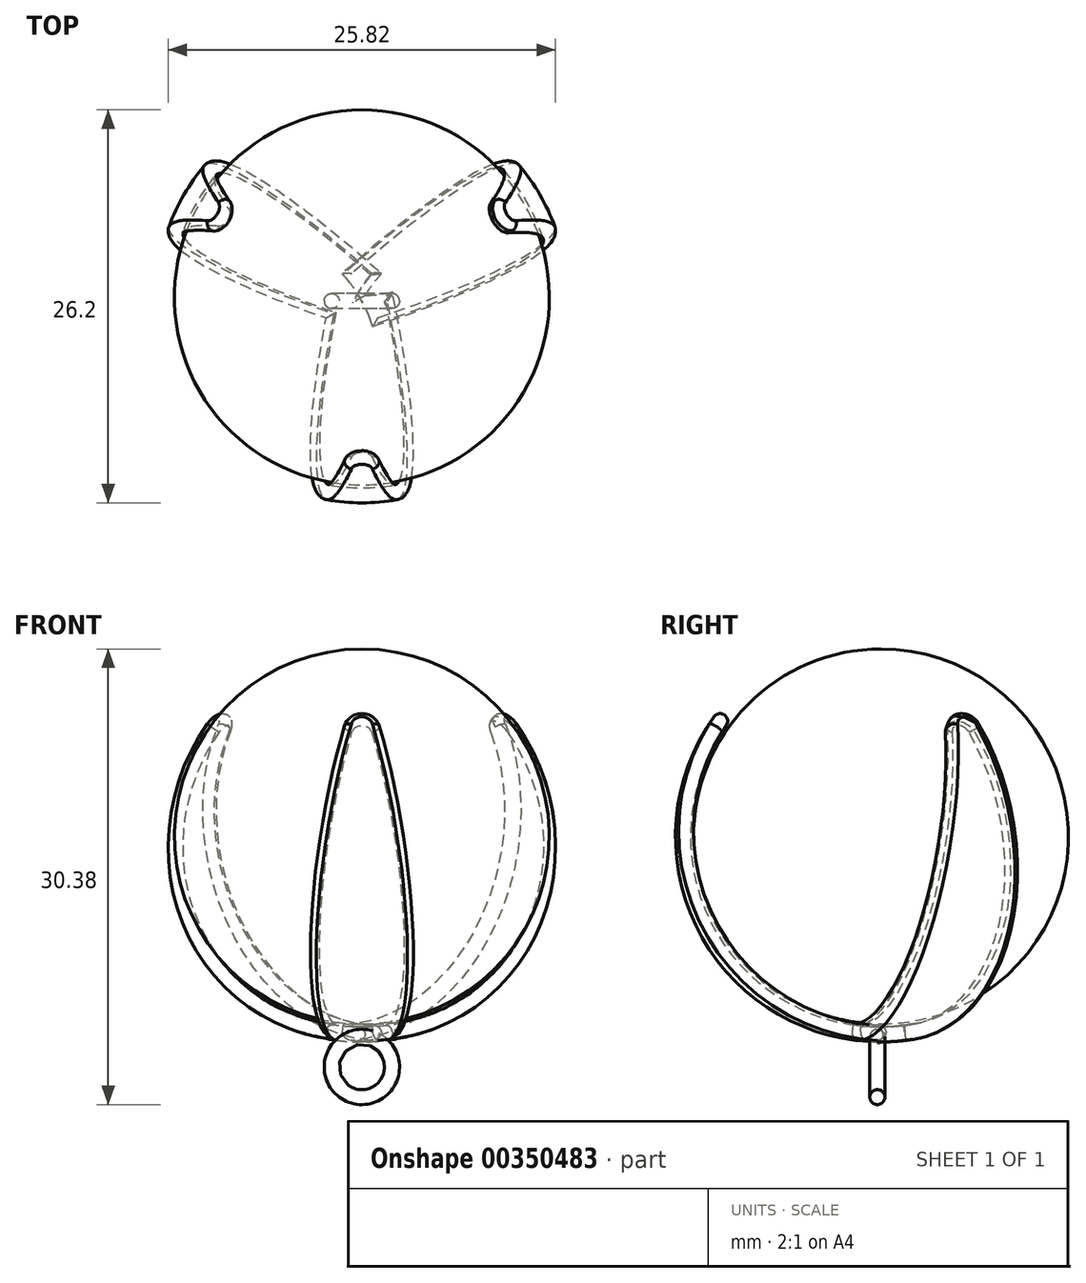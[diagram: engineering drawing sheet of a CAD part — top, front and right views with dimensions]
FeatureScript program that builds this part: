
annotation { "Feature Type Name" : "Feature", "Feature Type Description" : "" }
export const myFeature = defineFeature(function(context is Context, id is Id, definition is map)
    precondition{}
    {
        {
            var Q0;
            Q0=qCreatedBy(makeId("Right.planeOp"),FACE);
            var sketch = newSketch(context, id + "F0", { "sketchPlane" : qUnion([Q0])});
            skArc(sketch, "E0", {"start": v(7.54, -10.22) * mm, "mid": v(0, 12.7) * mm, "end": v(-7.54, -10.22) * mm});
            skArc(sketch, "E1", {"start": v(8.14, -11.02) * mm, "mid": v(0, 13.7) * mm, "end": v(-8.14, -11.02) * mm});
            skLineSegment(sketch, "E2", {"start": v(-7.54, -10.22) * mm, "end": v(-8.14, -11.02) * mm});
            skLineSegment(sketch, "E3.MirrorCS", {"start": v(7.54, -10.22) * mm, "end": v(8.14, -11.02) * mm});
            skLineSegment(sketch, "E4", {"start": v(0, 26.64) * mm, "end": v(0, -24.08) * mm});
            skPoint(sketch, "E4.endSnap0", {"position": v(0, 12.7) * mm});
            skCircle(sketch, "E5", {"center": v(0, 0) * mm, "radius": 12.5 * mm});
            skSolve(sketch);
        }
        {
            var Q0;
            Q0=qCreatedBy(makeId("Top.planeOp"),FACE);
            var sketch = newSketch(context, id + "F1", { "sketchPlane" : qUnion([Q0])});
            skLineSegment(sketch, "E6", {"start": v(-16.75, 0) * mm, "end": v(30.7, 0) * mm, "construction": true});
            skSolve(sketch);
        }
        {
            var Q0;
            {var subQ0=sQuery(id+"F0.wireOp",EDGE,"E2");Q0=makeQuery(id+"F0.imprint","IMPRINT",FACE,{"disambiguationData":[TD([[makeQuery(id+"F0.imprint","IMPRINT",EDGE,{"derivedFrom":subQ0}),-1.0]])]});}
            var Q1;
            Q1=sQuery(id+"F0.wireOp",EDGE,"E4");
            revolve(context, id + "F2", {"entities" : qUnion([Q0]), "axis" : qUnion([Q1]), "revolveType" : RevolveType.SYMMETRIC, "angle" : 30 * degree});
        }
        {
            var Q0;
            Q0=makeQuery(id+"F2.opRevolve","SWEPT_BODY",BODY,{"disambiguationData":[OSD([sQuery(id+"F0.wireOp",EDGE,"E0"),sQuery(id+"F0.wireOp",EDGE,"E1"),sQuery(id+"F0.wireOp",EDGE,"E2"),sQuery(id+"F0.wireOp",EDGE,"E4")])]});
            var Q1;
            Q1=sQuery(id+"F1.wireOp",EDGE,"E6");
            transform(context, id + "F3", {"entities" : qUnion([Q0]), "transformType" : TransformType.ROTATION, "transformAxis" : qUnion([Q1]), "angle" : 37 * degree, "makeCopy" : false});
        }
        {
            var Q0;
            Q0=makeQuery(id+"F2.opRevolve","SWEPT_BODY",BODY,{"disambiguationData":[OSD([sQuery(id+"F0.wireOp",EDGE,"E0"),sQuery(id+"F0.wireOp",EDGE,"E1"),sQuery(id+"F0.wireOp",EDGE,"E2"),sQuery(id+"F0.wireOp",EDGE,"E4")])]});
            var Q1;
            Q1=sQuery(id+"F0.wireOp",EDGE,"E4");
            circularPattern(context, id + "F4", {"entities" : qUnion([Q0]), "axis" : qUnion([Q1]), "angle" : 360 * degree, "instanceCount" : 3, "equalSpace" : true, "computeTransformsWithoutBuiltin" : true});
        }
        {
            var Q0;
            Q0=makeQuery(id+"F2.opRevolve","SWEPT_BODY",BODY,{"disambiguationData":[OSD([sQuery(id+"F0.wireOp",EDGE,"E0"),sQuery(id+"F0.wireOp",EDGE,"E1"),sQuery(id+"F0.wireOp",EDGE,"E2"),sQuery(id+"F0.wireOp",EDGE,"E4")])]});
            var Q1;
            Q1=makeQuery(id+"F4.opPattern","COPY",BODY,{"derivedFrom":makeQuery(id+"F2.opRevolve","SWEPT_BODY",BODY,{"disambiguationData":[OSD([sQuery(id+"F0.wireOp",EDGE,"E0"),sQuery(id+"F0.wireOp",EDGE,"E1"),sQuery(id+"F0.wireOp",EDGE,"E2"),sQuery(id+"F0.wireOp",EDGE,"E4")])]}),"instanceName":"1"});
            booleanBodies(context, id + "F5", {"operationType" : BooleanOperationType.UNION, "tools" : qUnion([Q0, Q1])});
        }
        {
            var Q0;
            Q0=makeQuery(id+"F4.opPattern","COPY",EDGE,{"derivedFrom":makeQuery(id+"F2.opRevolve","CAP_EDGE",EDGE,{"disambiguationData":[OSD([sQuery(id+"F0.wireOp",EDGE,"E4")])],"isStart":true}),"instanceName":"1"});
            var Q1;
            Q1=makeQuery(id+"F2.opRevolve","CAP_EDGE",EDGE,{"disambiguationData":[OSD([sQuery(id+"F0.wireOp",EDGE,"E4")])],"isStart":true});
            var Q2;
            Q2=makeQuery(id+"F4.opPattern","COPY",EDGE,{"derivedFrom":makeQuery(id+"F2.opRevolve","CAP_EDGE",EDGE,{"disambiguationData":[OSD([sQuery(id+"F0.wireOp",EDGE,"E4")])],"isStart":true}),"instanceName":"2"});
            fillet(context, id + "F6", {"entities" : qUnion([Q0, Q1, Q2]), "radius" : 1.2 * mm, "tangentPropagation" : true, "allowEdgeOverflow" : false});
        }
        {
            var Q0;
            {var subQ0=makeQuery(id+"F2.opRevolve","SWEPT_FACE",FACE,{"disambiguationData":[OSD([sQuery(id+"F0.wireOp",EDGE,"E1")])]});Q0=makeQuery(id+"F5.opBoolean","MERGE",FACE,{"derivedFrom":[subQ0,makeQuery(id+"F4.opPattern","COPY",FACE,{"derivedFrom":subQ0,"instanceName":"1"})]});}
            var Q1;
            {var subQ0=makeQuery(id+"F2.opRevolve","SWEPT_FACE",FACE,{"disambiguationData":[OSD([sQuery(id+"F0.wireOp",EDGE,"E0")])]});Q1=makeQuery(id+"F5.opBoolean","MERGE",FACE,{"derivedFrom":[subQ0,makeQuery(id+"F4.opPattern","COPY",FACE,{"derivedFrom":subQ0,"instanceName":"1"})]});}
            var Q2;
            Q2=makeQuery(id+"F4.opPattern","COPY",FACE,{"derivedFrom":makeQuery(id+"F2.opRevolve","SWEPT_FACE",FACE,{"disambiguationData":[OSD([sQuery(id+"F0.wireOp",EDGE,"E1")])]}),"instanceName":"2"});
            fillet(context, id + "F7", {"entities" : qUnion([Q0, Q1, Q2]), "radius" : 0.5 * mm, "tangentPropagation" : true, "allowEdgeOverflow" : false});
        }
        {
            var Q0;
            Q0=qCreatedBy(makeId("Front.planeOp"),FACE);
            var sketch = newSketch(context, id + "F8", { "sketchPlane" : qUnion([Q0])});
            skCircle(sketch, "E7", {"center": v(0.24, -13.36) * mm, "radius": 0.5 * mm});
            skLineSegment(sketch, "E8", {"start": v(2.52, -15.37) * mm, "end": v(-3.13, -15.37) * mm, "construction": true});
            skSolve(sketch);
        }
        {
            var Q0;
            Q0=makeQuery(id+"F8.imprint","IMPRINT",FACE,{"disambiguationData":[TD([[makeQuery(id+"F8.imprint","IMPRINT",EDGE,{"derivedFrom":sQuery(id+"F8.wireOp",EDGE,"E7")}),1.0]])]});
            var Q1;
            Q1=sQuery(id+"F8.wireOp",EDGE,"E8");
            revolve(context, id + "F9", {"entities" : qUnion([Q0]), "axis" : qUnion([Q1]), "revolveType" : RevolveType.FULL});
        }
        {
            var Q0;
            Q0=makeQuery(id+"F9.opRevolve","SWEPT_BODY",BODY,{"disambiguationData":[OSD([sQuery(id+"F8.wireOp",EDGE,"E7")])]});
            var Q1;
            Q1=sQuery(id+"F0.wireOp",EDGE,"E4");
            transform(context, id + "F10", {"entities" : qUnion([Q0]), "transformType" : TransformType.ROTATION, "transformAxis" : qUnion([Q1]), "angle" : 90 * degree, "makeCopy" : false});
        }
        {
            var Q0;
            {var subQ0=sQuery(id+"F0.wireOp",EDGE,"E5");var subQ1=sQuery(id+"F0.wireOp",EDGE,"E4");var subQ2=makeQuery(id+"F0.imprint","INTERSECT",VERTEX,{"disambiguationData":[OD(0.0)],"derivedFrom":[subQ1,subQ0]});Q0=makeQuery(id+"F0.imprint","IMPRINT",FACE,{"disambiguationData":[TD([[makeQuery(id+"F0.imprint","IMPRINT",EDGE,{"disambiguationData":[TD([[subQ2,1.0]])],"derivedFrom":subQ1}),-1.0]])]});}
            var Q1;
            Q1=sQuery(id+"F0.wireOp",EDGE,"E4");
            revolve(context, id + "F11", {"entities" : qUnion([Q0]), "axis" : qUnion([Q1]), "revolveType" : RevolveType.FULL});
        }
    });
